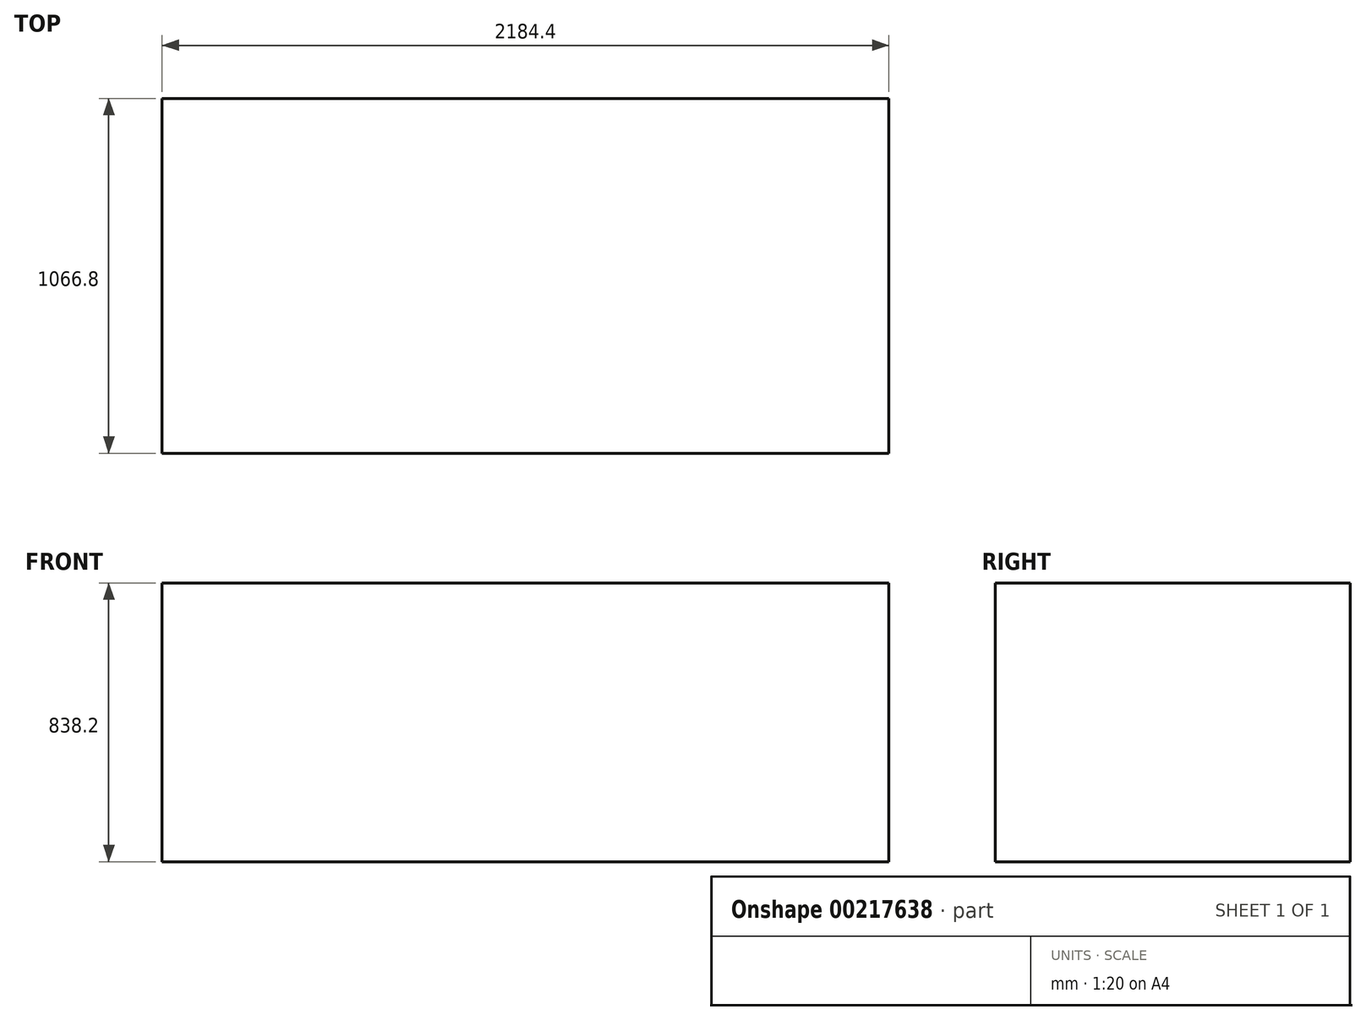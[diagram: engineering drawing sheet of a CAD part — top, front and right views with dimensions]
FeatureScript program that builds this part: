
annotation { "Feature Type Name" : "Feature", "Feature Type Description" : "" }
export const myFeature = defineFeature(function(context is Context, id is Id, definition is map)
    precondition{}
    {
        {
            var Q0;
            Q0=qCreatedBy(makeId("Top.planeOp"),FACE);
            var sketch = newSketch(context, id + "F0", { "sketchPlane" : qUnion([Q0])});
            skLineSegment(sketch, "E0.bottom", {"start": v(-1092.2, 533.4) * mm, "end": v(1092.2, 533.4) * mm});
            skLineSegment(sketch, "E0.top", {"start": v(-1092.2, -533.4) * mm, "end": v(1092.2, -533.4) * mm});
            skLineSegment(sketch, "E0.left", {"start": v(-1092.2, 533.4) * mm, "end": v(-1092.2, -533.4) * mm});
            skLineSegment(sketch, "E0.right", {"start": v(1092.2, 533.4) * mm, "end": v(1092.2, -533.4) * mm});
            skSolve(sketch);
        }
        {
            var Q0;
            Q0 = qSketchRegion(id + "F0", true);
            extrude(context, id + "F1", {"entities" : qUnion([Q0]), "depth" : 838.2 * mm});
        }
    });
